# Revit family: Thorn COLLEGE 2 Infill Panel
name_source: partatom
category: Lighting Fixtures
units: mm (PartAtom-declared; Revit-internal decimal feet)

## family parameters
Cut with Voids When Loaded = No
Host = Face
Light Source = No
Maintain Annotation Orientation = No
Part Type = Normal
Room Calculation Point = Yes
Round Connector Dimension = Use Diameter
Shared = No

## types (5) — shared parameters
Apparent Load = 25 VA
Assembly Code = Pr_70_60_48_45
Description = Surface / Suspended LED Luminaire
Luminaire Height = 82.32 mm  [stored 0.270079 ft]
Luminaire Width = 195.32 mm  [stored 0.640814 ft]
Manufacturer = Thorn Lighting
Type Image = COLLEGE 2 Infill Panel.jpg
URL = https://www.thornlighting.com
zero-valued in all types: Default Elevation

## per-type parameters (varying)
| type | Luminaire Length | Model |
| COLLEGE 2 1200MM INFILL PANEL | 1242 mm  [stored 4.0748 ft] | 96800191 |
| COLLEGE 2 300MM INFILL PANEL | 342 mm  [stored 1.12205 ft] | 96800188 |
| COLLEGE 2 600MM INFILL PANEL | 642 mm  [stored 2.1063 ft] | 96800189 |
| COLLEGE 2 900MM INFILL PANEL | 942 mm  [stored 3.09055 ft] | 96800190 |
| COLLEGE 2 1500MM INFILL PANEL | 1542 mm  [stored 5.05906 ft] | 96800192 |

note: [stored X ft] marks values corroborated as IEEE doubles in the binary element streams (Revit-internal decimal feet)

## geometry (parser evidence)
native form markers: Sweep x6
no freeform markers — native parametric forms only
